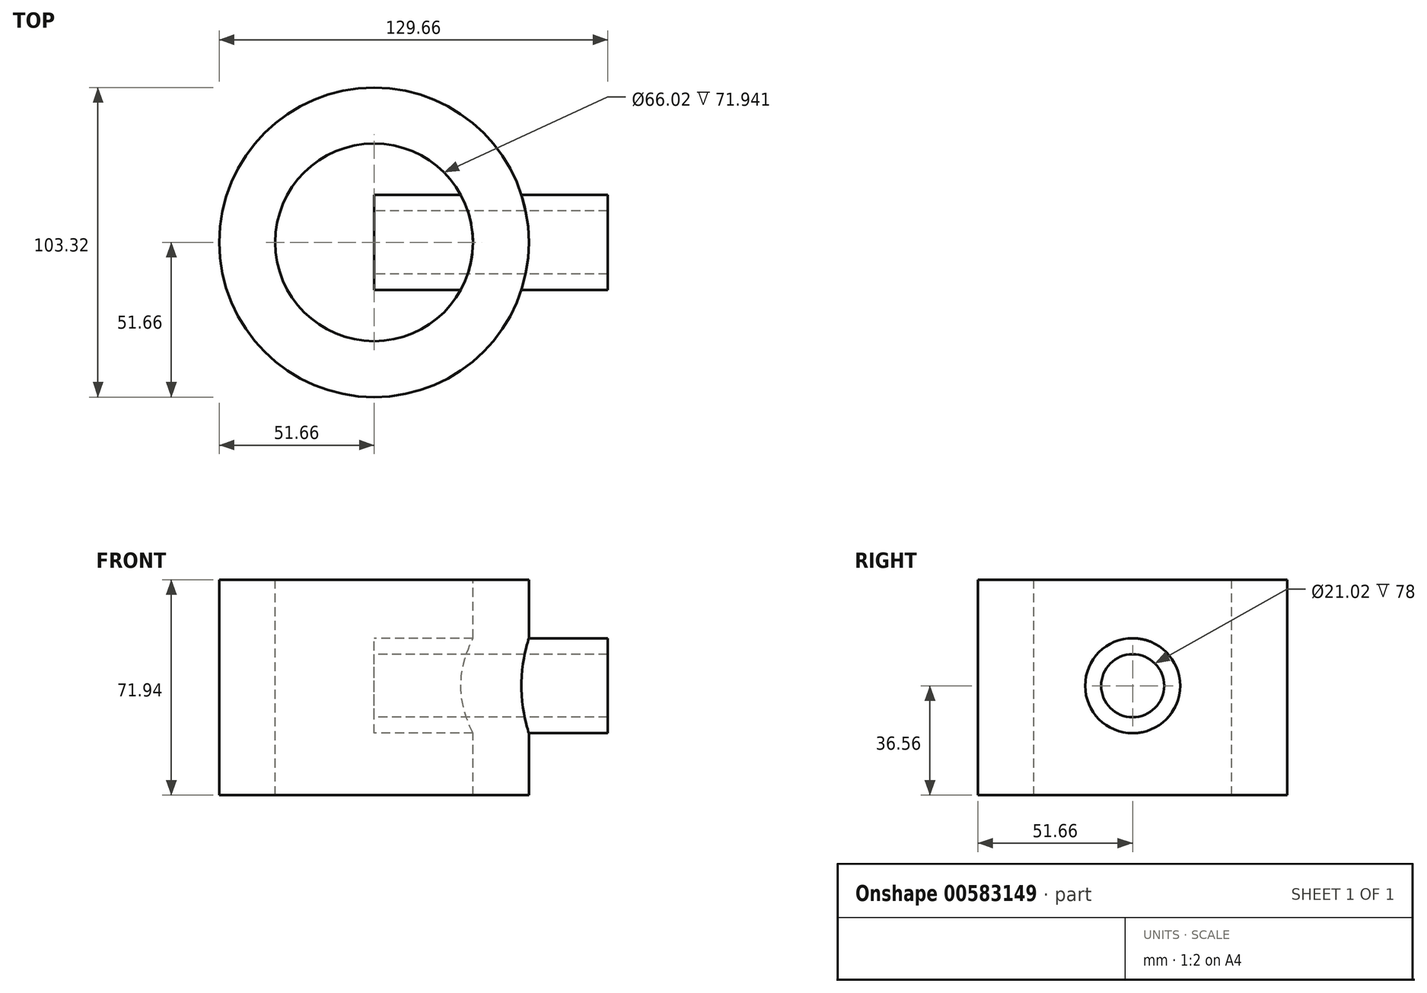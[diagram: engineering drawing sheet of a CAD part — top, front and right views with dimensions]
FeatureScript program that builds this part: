
annotation { "Feature Type Name" : "Feature", "Feature Type Description" : "" }
export const myFeature = defineFeature(function(context is Context, id is Id, definition is map)
    precondition{}
    {
        {
            var Q0;
            Q0=qCreatedBy(makeId("Front.planeOp"),FACE);
            var sketch = newSketch(context, id + "F0", { "sketchPlane" : qUnion([Q0])});
            skLineSegment(sketch, "E0", {"start": v(0, 64.69) * mm, "end": v(0, -50.18) * mm, "construction": true});
            skLineSegment(sketch, "E1.bottom", {"start": v(33, 35.38) * mm, "end": v(51.66, 35.38) * mm});
            skLineSegment(sketch, "E1.top", {"start": v(33, -36.56) * mm, "end": v(51.66, -36.56) * mm});
            skLineSegment(sketch, "E1.left", {"start": v(33, 35.38) * mm, "end": v(33, -36.56) * mm});
            skLineSegment(sketch, "E1.right", {"start": v(51.66, 35.38) * mm, "end": v(51.66, -36.56) * mm});
            skSolve(sketch);
        }
        {
            var Q0;
            Q0 = qSketchRegion(id + "F0", true);
            var Q1;
            Q1=sQuery(id+"F0.wireOp",EDGE,"E0");
            revolve(context, id + "F1", {"entities" : qUnion([Q0]), "axis" : qUnion([Q1]), "revolveType" : RevolveType.FULL});
        }
        {
            var Q0;
            Q0=qCreatedBy(makeId("Right.planeOp"),FACE);
            var sketch = newSketch(context, id + "F2", { "sketchPlane" : qUnion([Q0])});
            skCircle(sketch, "E2", {"center": v(0, 0) * mm, "radius": 15.85 * mm});
            skSolve(sketch);
        }
        {
            var Q0;
            Q0 = qSketchRegion(id + "F2", true);
            extrude(context, id + "F3", {"entities" : qUnion([Q0]), "operationType" : NewBodyOperationType.ADD, "depth" : 78 * mm, "offsetDistance" : 25 * mm});
        }
        {
            var Q0;
            Q0=qCreatedBy(makeId("Right.planeOp"),FACE);
            var sketch = newSketch(context, id + "F4", { "sketchPlane" : qUnion([Q0])});
            skCircle(sketch, "E3", {"center": v(0, 0) * mm, "radius": 10.51 * mm});
            skSolve(sketch);
        }
        {
            var Q0;
            Q0 = qSketchRegion(id + "F4", true);
            extrude(context, id + "F5", {"entities" : qUnion([Q0]), "operationType" : NewBodyOperationType.REMOVE, "depth" : 80 * mm, "offsetDistance" : 25 * mm});
        }
    });
